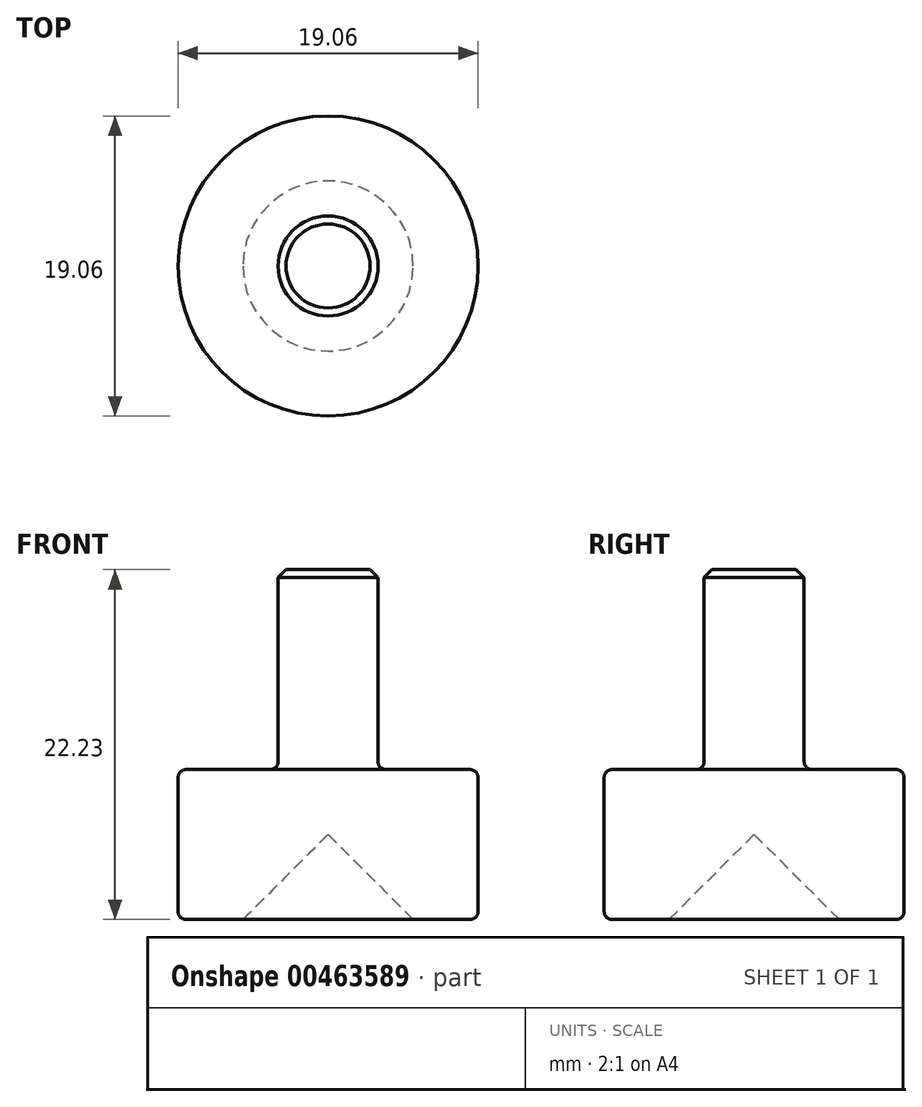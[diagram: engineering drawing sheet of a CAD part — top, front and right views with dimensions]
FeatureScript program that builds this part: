
annotation { "Feature Type Name" : "Feature", "Feature Type Description" : "" }
export const myFeature = defineFeature(function(context is Context, id is Id, definition is map)
    precondition{}
    {
        {
            var Q0;
            Q0=qCreatedBy(makeId("Front.planeOp"),FACE);
            var sketch = newSketch(context, id + "F0", { "sketchPlane" : qUnion([Q0])});
            skLineSegment(sketch, "E0", {"start": v(0, 5.4) * mm, "end": v(0, 22.23) * mm});
            skLineSegment(sketch, "E1", {"start": v(3.17, 22.23) * mm, "end": v(3.18, 9.52) * mm});
            skLineSegment(sketch, "E2", {"start": v(0, 22.23) * mm, "end": v(3.17, 22.23) * mm});
            skLineSegment(sketch, "E3", {"start": v(5.4, 0) * mm, "end": v(9.53, 0) * mm});
            skLineSegment(sketch, "E4", {"start": v(3.18, 9.53) * mm, "end": v(9.53, 9.53) * mm});
            skLineSegment(sketch, "E5", {"start": v(9.53, 9.53) * mm, "end": v(9.53, 0) * mm});
            skPoint(sketch, "E6.orphan", {"position": v(3.18, 0) * mm});
            skLineSegment(sketch, "E7", {"start": v(0, 29.8) * mm, "end": v(0, 5.4) * mm, "construction": true});
            skLineSegment(sketch, "E8", {"start": v(5.4, 0) * mm, "end": v(0, 5.4) * mm});
            skLineSegment(sketch, "E9.trimOffspring", {"start": v(0, 2.78) * mm, "end": v(0, 0) * mm, "construction": true});
            skSolve(sketch);
        }
        {
            var Q0;
            Q0=makeQuery(id+"F0.imprint","IMPRINT",FACE,{"disambiguationData":[TD([[makeQuery(id+"F0.imprint","IMPRINT",EDGE,{"derivedFrom":sQuery(id+"F0.wireOp",EDGE,"E0")}),-1.0]])]});
            var Q1;
            Q1=sQuery(id+"F0.wireOp",EDGE,"E7");
            revolve(context, id + "F1", {"entities" : qUnion([Q0]), "axis" : qUnion([Q1]), "revolveType" : RevolveType.FULL});
        }
        {
            var Q0;
            Q0=makeQuery(id+"F1.opRevolve","SWEPT_EDGE",EDGE,{"disambiguationData":[OSD([sQuery(id+"F0.wireOp",EDGE,"E1"),sQuery(id+"F0.wireOp",EDGE,"E2")])]});
            chamfer(context, id + "F2", {"entities" : qUnion([Q0]), "width" : 0.5 * mm, "tangentPropagation" : true});
        }
        {
            var Q0;
            Q0=makeQuery(id+"F1.opRevolve","SWEPT_EDGE",EDGE,{"disambiguationData":[OSD([sQuery(id+"F0.wireOp",EDGE,"E4"),sQuery(id+"F0.wireOp",EDGE,"E5")])]});
            var Q1;
            Q1=makeQuery(id+"F1.opRevolve","SWEPT_EDGE",EDGE,{"disambiguationData":[OSD([sQuery(id+"F0.wireOp",EDGE,"E1"),sQuery(id+"F0.wireOp",EDGE,"E4")])]});
            var Q2;
            Q2=makeQuery(id+"F1.opRevolve","SWEPT_EDGE",EDGE,{"disambiguationData":[OSD([sQuery(id+"F0.wireOp",EDGE,"E3"),sQuery(id+"F0.wireOp",EDGE,"E5")])]});
            fillet(context, id + "F3", {"entities" : qUnion([Q0, Q1, Q2]), "radius" : 0.5 * mm, "tangentPropagation" : true, "allowEdgeOverflow" : false});
        }
    });
